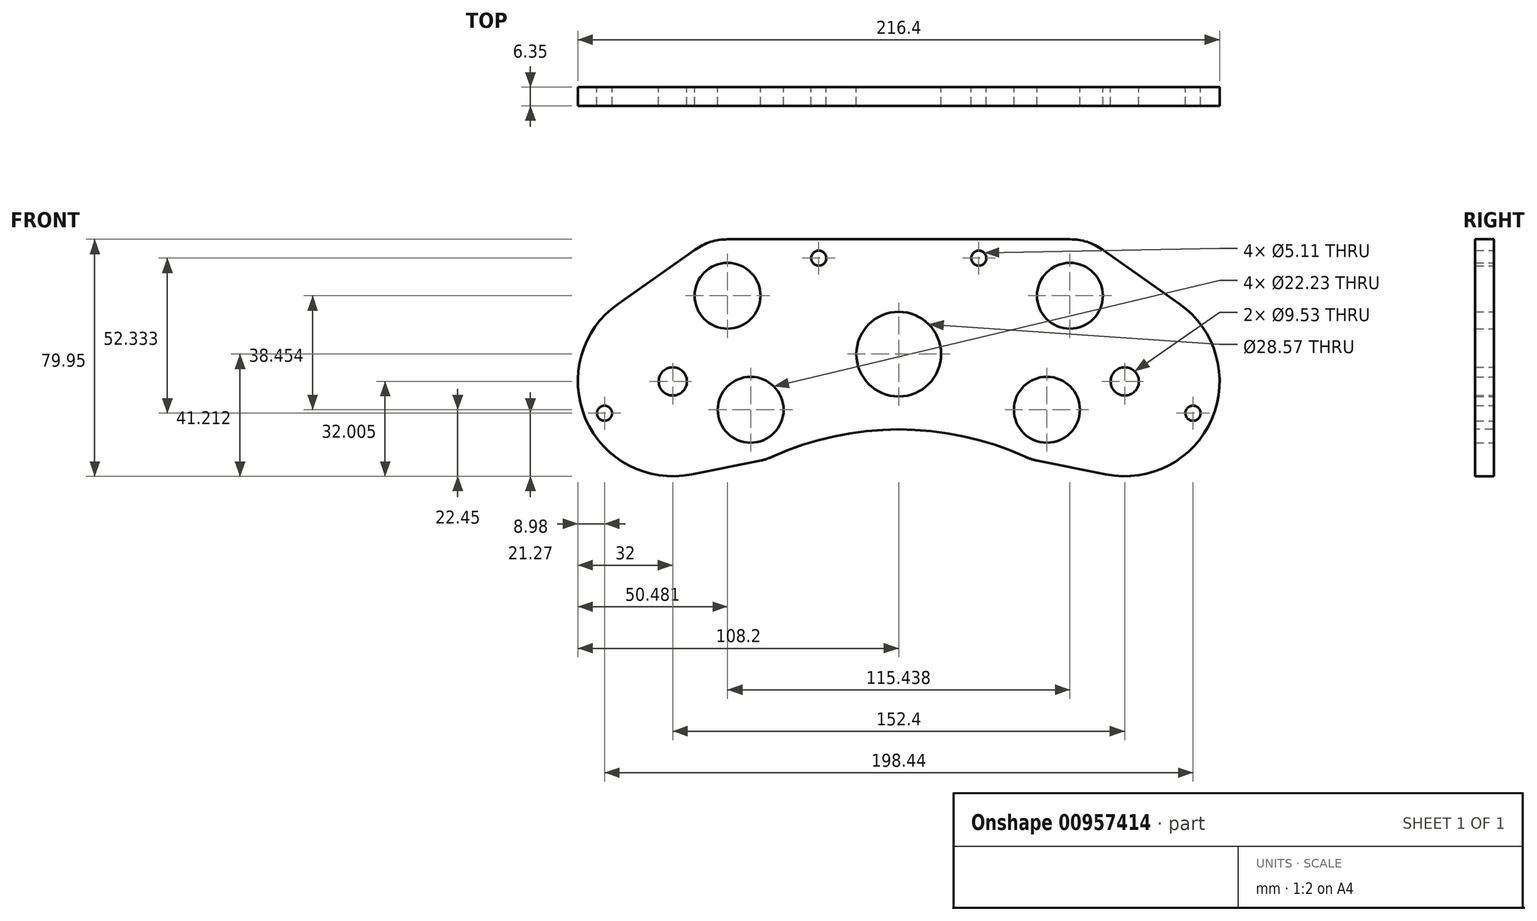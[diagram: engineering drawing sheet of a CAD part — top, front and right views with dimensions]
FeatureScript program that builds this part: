
annotation { "Feature Type Name" : "Feature", "Feature Type Description" : "" }
export const myFeature = defineFeature(function(context is Context, id is Id, definition is map)
    precondition{}
    {
        {
            var Q0;
            Q0=qCreatedBy(makeId("Front.planeOp"),FACE);
            var sketch = newSketch(context, id + "F0", { "sketchPlane" : qUnion([Q0])});
            skCircle(sketch, "E0", {"center": v(-76.2, 60.33) * mm, "radius": 32 * mm, "construction": true});
            skCircle(sketch, "E1", {"center": v(76.2, 60.33) * mm, "radius": 32 * mm, "construction": true});
            skLineSegment(sketch, "E2", {"start": v(-76.2, 60.33) * mm, "end": v(76.2, 60.32) * mm, "construction": true});
            skLineSegment(sketch, "E3", {"start": v(0, 60.33) * mm, "end": v(0, 0) * mm, "construction": true});
            skLineSegment(sketch, "E4.bottom", {"start": v(-101.6, -25.4) * mm, "end": v(101.6, -25.4) * mm, "construction": true});
            skLineSegment(sketch, "E4.top", {"start": v(-101.6, 25.4) * mm, "end": v(101.6, 25.4) * mm, "construction": true});
            skLineSegment(sketch, "E4.left", {"start": v(-101.6, -25.4) * mm, "end": v(-101.6, 25.4) * mm, "construction": true});
            skLineSegment(sketch, "E4.right", {"start": v(101.6, -25.4) * mm, "end": v(101.6, 25.4) * mm, "construction": true});
            skPoint(sketch, "E4.middle", {"position": v(0, 0) * mm});
            skCircle(sketch, "E5", {"center": v(0, -1.59) * mm, "radius": 50.8 * mm, "construction": true});
            skCircle(sketch, "E6", {"center": v(-76.2, 60.33) * mm, "radius": 7.62 * mm, "construction": true});
            skCircle(sketch, "E7", {"center": v(76.2, 60.33) * mm, "radius": 7.62 * mm, "construction": true});
            skCircle(sketch, "E8", {"center": v(0, 69.53) * mm, "radius": 34.3 * mm, "construction": true});
            skCircle(sketch, "E9", {"center": v(0, 69.53) * mm, "radius": 38.1 * mm, "construction": true});
            skCircle(sketch, "E10", {"center": v(0, -1.59) * mm, "radius": 33.02 * mm, "construction": true});
            skCircle(sketch, "E11", {"center": v(0, 69.53) * mm, "radius": 25.4 * mm, "construction": true});
            skCircle(sketch, "E12", {"center": v(0, -1.59) * mm, "radius": 45.72 * mm, "construction": true});
            skCircle(sketch, "E13", {"center": v(-76.2, 60.33) * mm, "radius": 8.9 * mm, "construction": true});
            skCircle(sketch, "E14", {"center": v(76.2, 60.33) * mm, "radius": 8.9 * mm, "construction": true});
            skCircle(sketch, "E15", {"center": v(0, 69.53) * mm, "radius": 14.29 * mm});
            skCircle(sketch, "E16", {"center": v(0, -1.59) * mm, "radius": 14.29 * mm, "construction": true});
            skCircle(sketch, "E17", {"center": v(-88.9, 12.7) * mm, "radius": 2.55 * mm, "construction": true});
            skCircle(sketch, "E18.0.1.0", {"center": v(-88.9, -12.7) * mm, "radius": 2.55 * mm, "construction": true});
            skCircle(sketch, "E18.1.0.0", {"center": v(-63.5, 12.7) * mm, "radius": 2.55 * mm, "construction": true});
            skCircle(sketch, "E18.1.1.0", {"center": v(-63.5, -12.7) * mm, "radius": 2.55 * mm, "construction": true});
            skCircle(sketch, "E18.2.0.0", {"center": v(-38.1, 12.7) * mm, "radius": 2.55 * mm});
            skCircle(sketch, "E18.2.1.0", {"center": v(-38.1, -12.7) * mm, "radius": 2.55 * mm});
            skCircle(sketch, "E18.3.0.0", {"center": v(-12.7, 12.7) * mm, "radius": 2.55 * mm, "construction": true});
            skCircle(sketch, "E18.3.1.0", {"center": v(-12.7, -12.7) * mm, "radius": 2.55 * mm, "construction": true});
            skCircle(sketch, "E18.4.0.0", {"center": v(12.7, 12.7) * mm, "radius": 2.55 * mm, "construction": true});
            skCircle(sketch, "E18.4.1.0", {"center": v(12.7, -12.7) * mm, "radius": 2.55 * mm, "construction": true});
            skCircle(sketch, "E18.5.0.0", {"center": v(38.1, 12.7) * mm, "radius": 2.55 * mm});
            skCircle(sketch, "E18.5.1.0", {"center": v(38.1, -12.7) * mm, "radius": 2.55 * mm});
            skCircle(sketch, "E18.6.0.0", {"center": v(63.5, 12.7) * mm, "radius": 2.55 * mm, "construction": true});
            skCircle(sketch, "E18.6.1.0", {"center": v(63.5, -12.7) * mm, "radius": 2.55 * mm, "construction": true});
            skCircle(sketch, "E18.7.0.0", {"center": v(88.9, 12.7) * mm, "radius": 2.55 * mm, "construction": true});
            skCircle(sketch, "E18.7.1.0", {"center": v(88.9, -12.7) * mm, "radius": 2.55 * mm, "construction": true});
            skLineSegment(sketch, "E18.direction1", {"start": v(-88.9, 12.7) * mm, "end": v(-63.5, 12.7) * mm, "construction": true});
            skLineSegment(sketch, "E18.direction2", {"start": v(-88.9, 12.7) * mm, "end": v(-88.9, -12.7) * mm, "construction": true});
            skArc(sketch, "E19", {"start": v(-99.01, 37.88) * mm, "mid": v(-108.08, 63.18) * mm, "end": v(-94.65, 86.47) * mm});
            skCircle(sketch, "E20", {"center": v(-76.2, 60.33) * mm, "radius": 4.76 * mm});
            skCircle(sketch, "E21", {"center": v(76.2, 60.33) * mm, "radius": 4.76 * mm});
            skLineSegment(sketch, "E22", {"start": v(-99.22, 49.6) * mm, "end": v(-76.2, 60.33) * mm, "construction": true});
            skLineSegment(sketch, "E23", {"start": v(-76.2, 60.33) * mm, "end": v(-53.18, 71.06) * mm, "construction": true});
            skCircle(sketch, "E24", {"center": v(-53.18, 71.06) * mm, "radius": 2.55 * mm, "construction": true});
            skCircle(sketch, "E25", {"center": v(-99.22, 49.6) * mm, "radius": 2.55 * mm});
            skCircle(sketch, "E26.MirrorC", {"center": v(53.18, 71.06) * mm, "radius": 2.55 * mm, "construction": true});
            skLineSegment(sketch, "E27.MirrorCS", {"start": v(76.2, 60.33) * mm, "end": v(53.18, 71.06) * mm, "construction": true});
            skLineSegment(sketch, "E28.MirrorCS", {"start": v(99.22, 49.6) * mm, "end": v(76.2, 60.33) * mm, "construction": true});
            skCircle(sketch, "E29.MirrorC", {"center": v(99.22, 49.6) * mm, "radius": 2.55 * mm});
            skCircle(sketch, "E30", {"center": v(0, -1.59) * mm, "radius": 23.81 * mm, "construction": true});
            skArc(sketch, "E31", {"start": v(3.03, -25.2) * mm, "mid": v(0, -25.4) * mm, "end": v(-3.03, -25.2) * mm});
            skCircle(sketch, "E32", {"center": v(-38.1, -12.7) * mm, "radius": 7.94 * mm, "construction": true});
            skCircle(sketch, "E33", {"center": v(38.1, -12.7) * mm, "radius": 7.94 * mm, "construction": true});
            skLineSegment(sketch, "E34", {"start": v(-3.03, -25.2) * mm, "end": v(-39.11, -20.57) * mm});
            skArc(sketch, "E35", {"start": v(-39.11, -20.57) * mm, "mid": v(-41.63, -19.81) * mm, "end": v(-43.76, -18.27) * mm});
            skLineSegment(sketch, "E36", {"start": v(-43.76, -18.27) * mm, "end": v(-99.01, 37.88) * mm});
            skLineSegment(sketch, "E37", {"start": v(3.03, -25.2) * mm, "end": v(39.11, -20.57) * mm});
            skArc(sketch, "E38", {"start": v(39.11, -20.57) * mm, "mid": v(41.63, -19.81) * mm, "end": v(43.76, -18.27) * mm});
            skLineSegment(sketch, "E39", {"start": v(43.76, -18.27) * mm, "end": v(99.01, 37.88) * mm});
            skCircle(sketch, "E40", {"center": v(-57.72, 89.22) * mm, "radius": 26.68 * mm, "construction": true});
            skCircle(sketch, "E41", {"center": v(-49.94, 50.77) * mm, "radius": 19.05 * mm, "construction": true});
            skCircle(sketch, "E42", {"center": v(57.72, 89.22) * mm, "radius": 26.68 * mm, "construction": true});
            skCircle(sketch, "E43", {"center": v(49.94, 50.77) * mm, "radius": 19.05 * mm, "construction": true});
            skCircle(sketch, "E44", {"center": v(-57.72, 89.22) * mm, "radius": 11.11 * mm});
            skCircle(sketch, "E45", {"center": v(-49.94, 50.77) * mm, "radius": 11.11 * mm});
            skCircle(sketch, "E46", {"center": v(49.94, 50.77) * mm, "radius": 11.11 * mm});
            skCircle(sketch, "E47", {"center": v(57.72, 89.22) * mm, "radius": 11.11 * mm});
            skCircle(sketch, "E48", {"center": v(57.72, 89.22) * mm, "radius": 19.05 * mm, "construction": true});
            skCircle(sketch, "E49", {"center": v(-57.72, 89.22) * mm, "radius": 19.05 * mm, "construction": true});
            skLineSegment(sketch, "E50", {"start": v(-57.72, 108.27) * mm, "end": v(57.72, 108.27) * mm});
            skArc(sketch, "E51", {"start": v(-57.72, 108.27) * mm, "mid": v(-63.48, 107.38) * mm, "end": v(-68.7, 104.79) * mm});
            skLineSegment(sketch, "E52", {"start": v(-68.7, 104.79) * mm, "end": v(-94.65, 86.47) * mm});
            skArc(sketch, "E53", {"start": v(57.72, 108.27) * mm, "mid": v(63.48, 107.38) * mm, "end": v(68.7, 104.79) * mm});
            skArc(sketch, "E54", {"start": v(99.01, 37.88) * mm, "mid": v(108.08, 63.18) * mm, "end": v(94.65, 86.47) * mm});
            skLineSegment(sketch, "E55", {"start": v(94.65, 86.47) * mm, "end": v(68.7, 104.79) * mm});
            skCircle(sketch, "E56", {"center": v(-49.94, 50.77) * mm, "radius": 17.46 * mm, "construction": true});
            skCircle(sketch, "E57", {"center": v(49.94, 50.77) * mm, "radius": 17.46 * mm, "construction": true});
            skLineSegment(sketch, "E58", {"start": v(-26.99, 101.92) * mm, "end": v(26.99, 101.92) * mm, "construction": true});
            skLineSegment(sketch, "E59", {"start": v(0, 101.92) * mm, "end": v(0, 69.53) * mm, "construction": true});
            skCircle(sketch, "E60", {"center": v(-26.99, 101.92) * mm, "radius": 2.55 * mm});
            skCircle(sketch, "E61", {"center": v(26.99, 101.92) * mm, "radius": 2.55 * mm});
            skCircle(sketch, "E62", {"center": v(26.99, 101.92) * mm, "radius": 6.35 * mm, "construction": true});
            skCircle(sketch, "E63", {"center": v(-26.99, 101.92) * mm, "radius": 6.35 * mm, "construction": true});
            skSolve(sketch);
        }
        {
            var Q0;
            Q0=qSketchRegion(id+"F0",true);
            extrude(context, id + "F1", {"entities" : qUnion([Q0]), "depth" : 6.35 * mm, "offsetDistance" : 25.4 * mm});
        }
        {
            var Q0;
            Q0=makeQuery(id+"F1.opExtrude","CAP_FACE",FACE,{"disambiguationData":[OSD([sQuery(id+"F0.wireOp",EDGE,"E15"),sQuery(id+"F0.wireOp",EDGE,"E18.2.0.0"),sQuery(id+"F0.wireOp",EDGE,"E18.2.1.0"),sQuery(id+"F0.wireOp",EDGE,"E18.5.0.0"),sQuery(id+"F0.wireOp",EDGE,"E18.5.1.0"),sQuery(id+"F0.wireOp",EDGE,"E19"),sQuery(id+"F0.wireOp",EDGE,"E20"),sQuery(id+"F0.wireOp",EDGE,"E21"),sQuery(id+"F0.wireOp",EDGE,"E31"),sQuery(id+"F0.wireOp",EDGE,"E34"),sQuery(id+"F0.wireOp",EDGE,"E35"),sQuery(id+"F0.wireOp",EDGE,"E36"),sQuery(id+"F0.wireOp",EDGE,"E37"),sQuery(id+"F0.wireOp",EDGE,"E38"),sQuery(id+"F0.wireOp",EDGE,"E39"),sQuery(id+"F0.wireOp",EDGE,"E44"),sQuery(id+"F0.wireOp",EDGE,"E45"),sQuery(id+"F0.wireOp",EDGE,"E46"),sQuery(id+"F0.wireOp",EDGE,"E47"),sQuery(id+"F0.wireOp",EDGE,"E50"),sQuery(id+"F0.wireOp",EDGE,"E51"),sQuery(id+"F0.wireOp",EDGE,"E52"),sQuery(id+"F0.wireOp",EDGE,"E53"),sQuery(id+"F0.wireOp",EDGE,"E54"),sQuery(id+"F0.wireOp",EDGE,"E55")])],"isStart":false});
            var sketch = newSketch(context, id + "F2", { "sketchPlane" : qUnion([Q0])});
            skArc(sketch, "E64", {"start": v(-99.01, 37.88) * mm, "mid": v(-85.58, 29.73) * mm, "end": v(-69.9, 28.95) * mm});
            skArc(sketch, "E65", {"start": v(69.9, 28.95) * mm, "mid": v(85.58, 29.73) * mm, "end": v(99.01, 37.88) * mm});
            skLineSegment(sketch, "E66", {"start": v(-99.01, 37.88) * mm, "end": v(-99.01, -25.4) * mm});
            skLineSegment(sketch, "E67", {"start": v(-99.01, -25.4) * mm, "end": v(99.01, -25.4) * mm});
            skLineSegment(sketch, "E68", {"start": v(99.01, -25.4) * mm, "end": v(99.01, 37.88) * mm});
            skArc(sketch, "E69", {"start": v(-46.5, 33.65) * mm, "mid": v(-44.57, 34.15) * mm, "end": v(-42.71, 34.87) * mm});
            skArc(sketch, "E70", {"start": v(42.71, 34.87) * mm, "mid": v(0, 44.13) * mm, "end": v(-42.71, 34.87) * mm});
            skArc(sketch, "E71", {"start": v(42.71, 34.87) * mm, "mid": v(44.57, 34.15) * mm, "end": v(46.5, 33.65) * mm});
            skPoint(sketch, "E72.visualSharp", {"position": v(56.94, 34.77) * mm});
            skPoint(sketch, "E73.visualSharp", {"position": v(-56.94, 34.77) * mm});
            skLineSegment(sketch, "E74", {"start": v(-69.9, 28.95) * mm, "end": v(-46.5, 33.65) * mm});
            skLineSegment(sketch, "E75", {"start": v(46.5, 33.65) * mm, "end": v(69.9, 28.95) * mm});
            skSolve(sketch);
        }
        {
            var Q0;
            Q0 = qSketchRegion(id + "F2", true);
            extrude(context, id + "F3", {"entities" : qUnion([Q0]), "operationType" : NewBodyOperationType.REMOVE, "oppositeDirection" : true, "depth" : 25.4 * mm, "offsetDistance" : 25.4 * mm});
        }
    });
